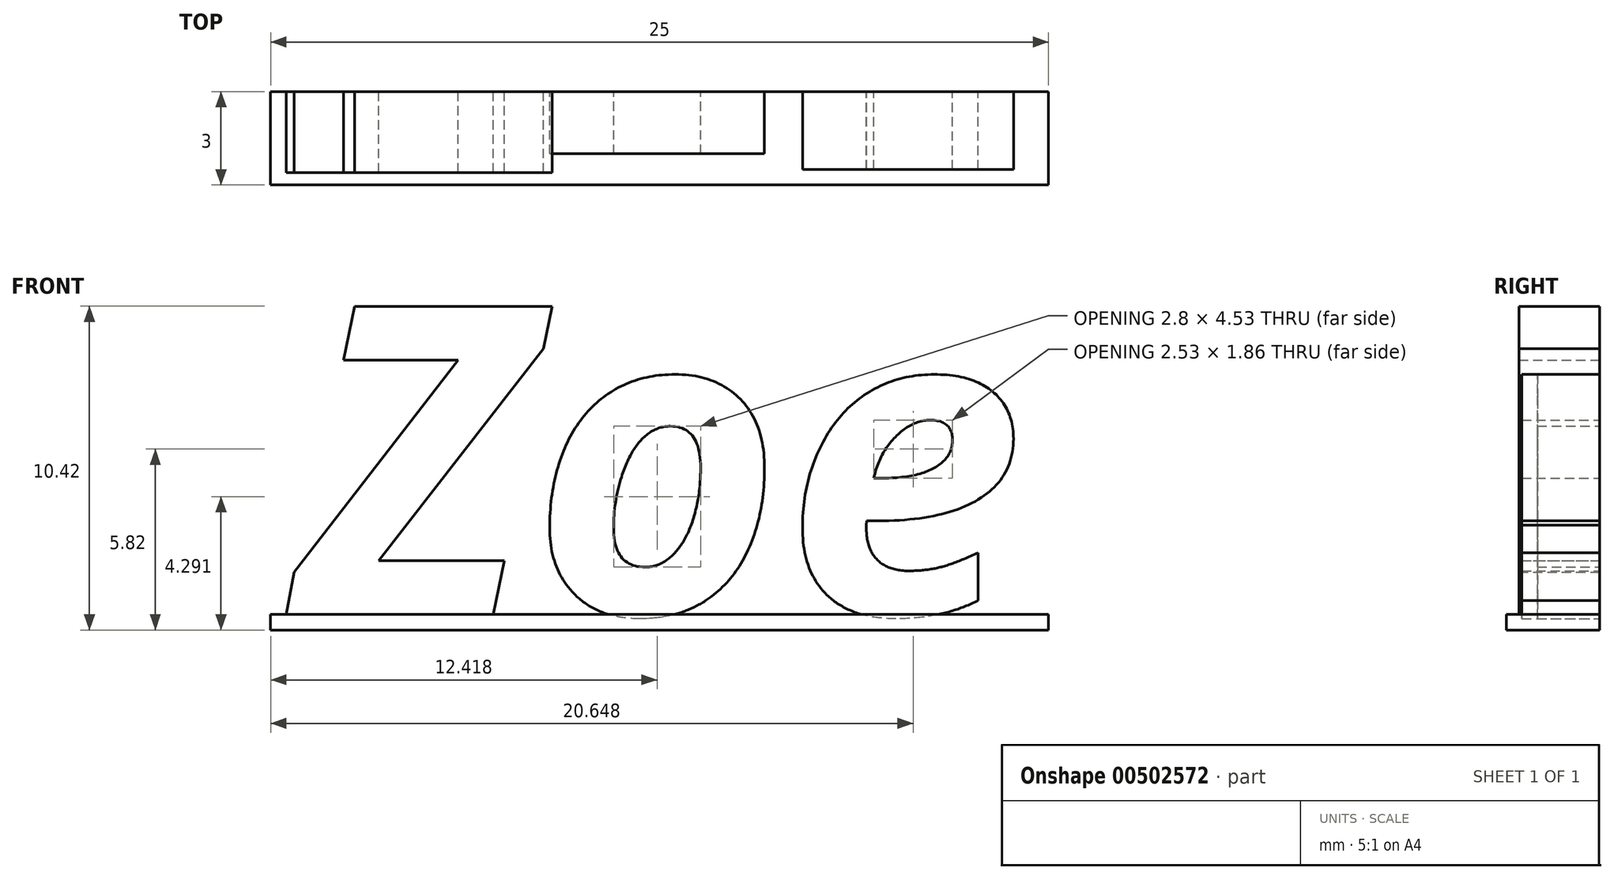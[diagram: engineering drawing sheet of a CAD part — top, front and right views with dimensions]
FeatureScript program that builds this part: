
annotation { "Feature Type Name" : "Feature", "Feature Type Description" : "" }
export const myFeature = defineFeature(function(context is Context, id is Id, definition is map)
    precondition{}
    {
        {
            var Q0;
            Q0=qCreatedBy(makeId("Front.planeOp"),FACE);
            var sketch = newSketch(context, id + "F0", { "sketchPlane" : qUnion([Q0])});
            skText(sketch, "E0", { "text": "Zoe", "fontName": "OpenSans-BoldItalic.ttf"});
            const initialGuessF0  = {"E0": [0, 0, 1, 0, 0.01]};
            skSetInitialGuess(sketch, initialGuessF0);
            skSolve(sketch);
        }
        {
            var Q0;
            Q0=makeQuery(id+"F0.imprint","IMPRINT",FACE,{"disambiguationData":[TD([[makeQuery(id+"F0.imprint","IMPRINT",EDGE,{"derivedFrom":sQuery(id+"F0.wireOp",EDGE,"E0.sketch_text.stroke-0")}),-1.0]])]});
            extrude(context, id + "F1", {"entities" : qUnion([Q0]), "depth" : 2.6 * mm, "offsetDistance" : 25 * mm});
        }
        {
            var Q0;
            Q0=makeQuery(id+"F0.imprint","IMPRINT",FACE,{"disambiguationData":[TD([[makeQuery(id+"F0.imprint","IMPRINT",EDGE,{"derivedFrom":sQuery(id+"F0.wireOp",EDGE,"E0.sketch_text.stroke-10")}),-1.0]])]});
            extrude(context, id + "F2", {"entities" : qUnion([Q0]), "depth" : 2 * mm, "offsetDistance" : 25 * mm});
        }
        {
            var Q0;
            Q0=makeQuery(id+"F0.imprint","IMPRINT",FACE,{"disambiguationData":[TD([[makeQuery(id+"F0.imprint","IMPRINT",EDGE,{"derivedFrom":sQuery(id+"F0.wireOp",EDGE,"E0.sketch_text.stroke-28")}),-1.0]])]});
            extrude(context, id + "F3", {"entities" : qUnion([Q0]), "depth" : 2.5 * mm, "offsetDistance" : 25 * mm});
        }
        {
            var Q0;
            Q0=qCreatedBy(makeId("Front.planeOp"),FACE);
            var sketch = newSketch(context, id + "F4", { "sketchPlane" : qUnion([Q0])});
            skLineSegment(sketch, "E1.bottom", {"start": v(-0.91, 0) * mm, "end": v(24.09, 0) * mm});
            skLineSegment(sketch, "E1.top", {"start": v(-0.91, -0.5) * mm, "end": v(24.09, -0.5) * mm});
            skLineSegment(sketch, "E1.left", {"start": v(-0.91, 0) * mm, "end": v(-0.91, -0.5) * mm});
            skLineSegment(sketch, "E1.right", {"start": v(24.09, 0) * mm, "end": v(24.09, -0.5) * mm});
            skSolve(sketch);
        }
        {
            var Q0;
            Q0=makeQuery(id+"F4.imprint","IMPRINT",FACE,{"disambiguationData":[TD([[makeQuery(id+"F4.imprint","IMPRINT",EDGE,{"derivedFrom":sQuery(id+"F4.wireOp",EDGE,"E1.bottom")}),-1.0]])]});
            extrude(context, id + "F5", {"entities" : qUnion([Q0]), "depth" : 3 * mm, "offsetDistance" : 25 * mm});
        }
    });
